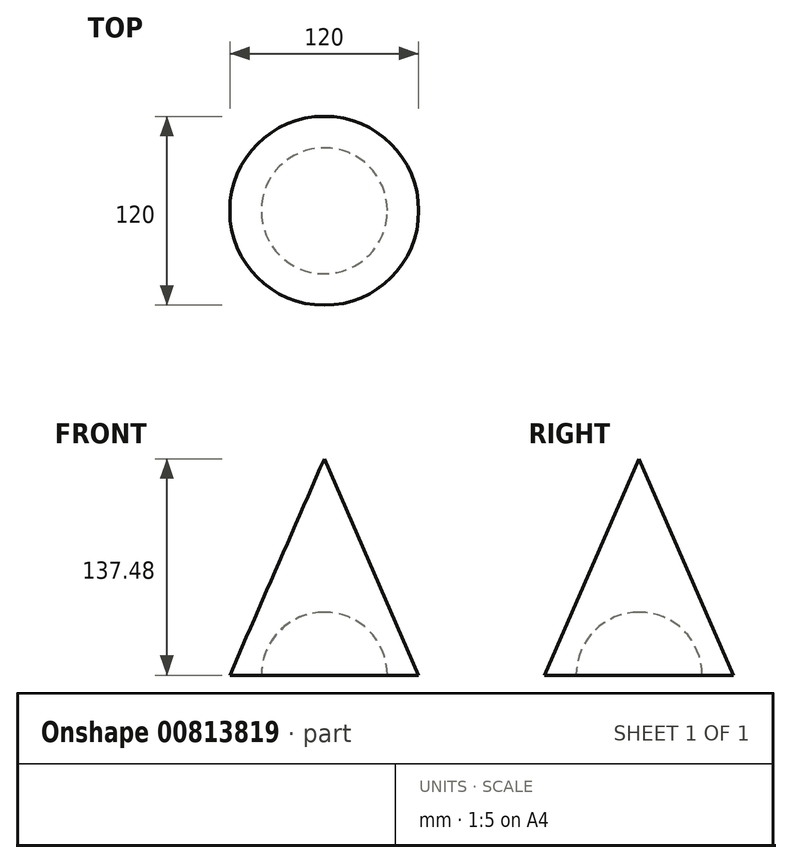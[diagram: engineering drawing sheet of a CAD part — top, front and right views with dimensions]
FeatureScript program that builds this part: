
annotation { "Feature Type Name" : "Feature", "Feature Type Description" : "" }
export const myFeature = defineFeature(function(context is Context, id is Id, definition is map)
    precondition{}
    {
        {
            var Q0;
            Q0=qCreatedBy(makeId("Front.planeOp"),FACE);
            var sketch = newSketch(context, id + "F0", { "sketchPlane" : qUnion([Q0])});
            skLineSegment(sketch, "E0", {"start": v(0, 0) * mm, "end": v(60, 0) * mm});
            skLineSegment(sketch, "E1", {"start": v(0, 0) * mm, "end": v(0, 137.48) * mm});
            skLineSegment(sketch, "E2", {"start": v(0, 137.48) * mm, "end": v(60, 0) * mm});
            skSolve(sketch);
        }
        {
            var Q0;
            Q0 = qSketchRegion(id + "F0", true);
            var Q1;
            Q1=sQuery(id+"F0.wireOp",EDGE,"E1");
            revolve(context, id + "F1", {"surfaceOperationType" : NewSurfaceOperationType.NEW, "entities" : qUnion([Q0]), "axis" : qUnion([Q1]), "revolveType" : RevolveType.FULL});
        }
        {
            var Q0;
            Q0=qCreatedBy(makeId("Front.planeOp"),FACE);
            var sketch = newSketch(context, id + "F2", { "sketchPlane" : qUnion([Q0])});
            skLineSegment(sketch, "E3", {"start": v(0, 0) * mm, "end": v(0, 40) * mm});
            skLineSegment(sketch, "E4", {"start": v(0, 0) * mm, "end": v(0, -40) * mm});
            skLineSegment(sketch, "E5", {"start": v(0, 0) * mm, "end": v(40, 0) * mm});
            skArc(sketch, "E6", {"start": v(0, -40) * mm, "mid": v(40, 0) * mm, "end": v(0, 40) * mm});
            skSolve(sketch);
        }
        {
            var Q0;
            Q0 = qSketchRegion(id + "F2", true);
            var Q1;
            Q1=sQuery(id+"F2.wireOp",EDGE,"E4");
            revolve(context, id + "F3", {"operationType" : NewBodyOperationType.REMOVE, "surfaceOperationType" : NewSurfaceOperationType.NEW, "entities" : qUnion([Q0]), "axis" : qUnion([Q1]), "revolveType" : RevolveType.FULL, "oppositeDirection" : true});
        }
    });
